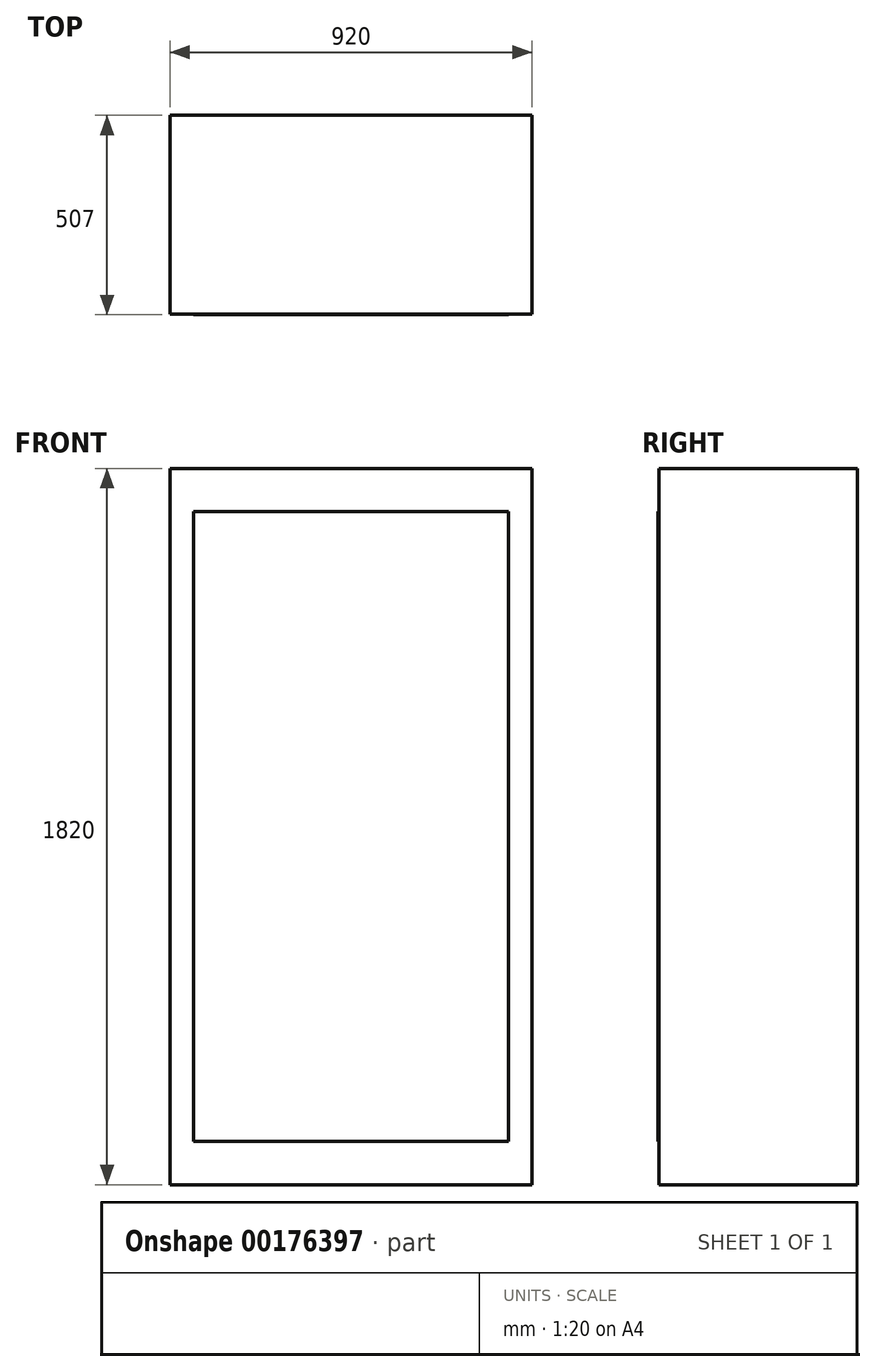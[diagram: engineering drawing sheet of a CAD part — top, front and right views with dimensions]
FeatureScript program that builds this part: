
annotation { "Feature Type Name" : "Feature", "Feature Type Description" : "" }
export const myFeature = defineFeature(function(context is Context, id is Id, definition is map)
    precondition{}
    {
        {
            var Q0;
            Q0=qCreatedBy(makeId("Front.planeOp"),FACE);
            var sketch = newSketch(context, id + "F2", { "sketchPlane" : qUnion([Q0])});
            skLineSegment(sketch, "E0.bottom", {"start": v(460, 910) * mm, "end": v(-460, 910) * mm});
            skLineSegment(sketch, "E0.top", {"start": v(460, -910) * mm, "end": v(-460, -910) * mm});
            skLineSegment(sketch, "E0.left", {"start": v(460, 910) * mm, "end": v(460, -910) * mm});
            skLineSegment(sketch, "E0.right", {"start": v(-460, 910) * mm, "end": v(-460, -910) * mm});
            skPoint(sketch, "E0.middle", {"position": v(0, 0) * mm});
            skSolve(sketch);
        }
        {
            var Q0;
            Q0=makeQuery(id+"F2.imprint","IMPRINT",FACE,{"disambiguationData":[TD([[makeQuery(id+"F2.imprint","IMPRINT",EDGE,{"derivedFrom":sQuery(id+"F2.wireOp",EDGE,"E0.bottom")}),1.0]])]});
            extrude(context, id + "F3", {"entities" : qUnion([Q0]), "depth" : 505 * mm});
        }
        {
            var Q0;
            Q0=makeQuery(id+"F3.opExtrude","CAP_FACE",FACE,{"disambiguationData":[OSD([sQuery(id+"F2.wireOp",EDGE,"E0.bottom"),sQuery(id+"F2.wireOp",EDGE,"E0.top"),sQuery(id+"F2.wireOp",EDGE,"E0.left"),sQuery(id+"F2.wireOp",EDGE,"E0.right")])],"isStart":false});
            var sketch = newSketch(context, id + "F0", { "sketchPlane" : qUnion([Q0])});
            skPoint(sketch, "E1.0", {"position": v(0, 0) * mm});
            skLineSegment(sketch, "E2.bottom", {"start": v(400, 800) * mm, "end": v(-400, 800) * mm});
            skLineSegment(sketch, "E2.top", {"start": v(400, -800) * mm, "end": v(-400, -800) * mm});
            skLineSegment(sketch, "E2.left", {"start": v(400, 800) * mm, "end": v(400, -800) * mm});
            skLineSegment(sketch, "E2.right", {"start": v(-400, 800) * mm, "end": v(-400, -800) * mm});
            skSolve(sketch);
        }
        {
            var Q0;
            Q0=makeQuery(id+"F0.imprint","IMPRINT",FACE,{"disambiguationData":[TD([[makeQuery(id+"F0.imprint","IMPRINT",EDGE,{"derivedFrom":sQuery(id+"F0.wireOp",EDGE,"E2.bottom")}),1.0]])]});
            extrude(context, id + "F1", {"entities" : qUnion([Q0]), "depth" : 2 * mm});
        }
    });
